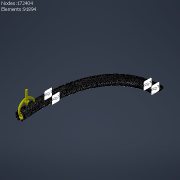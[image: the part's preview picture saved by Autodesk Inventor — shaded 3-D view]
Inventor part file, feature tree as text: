
AUTODESK INVENTOR PART (.ipt)
format: ipt  version: 2021 (Build 250183000, 183)  size: 282,624 bytes
history: native  units: mm
features: sketch x5, sweep x2, extrude x2, plane x2, split x1, hole x1
ambient origin geometry x8: Origin, YZ Plane, XZ Plane, XY Plane, X Axis, Y Axis, Z Axis, Center Point
bodies: Solid1 (feature_tree)
feature tree (13):
  sketch  "Sketch1"  dims[d0=3300.0mm d1=1650.0mm]
  sweep  "Sweep1"
  sweep  "Sweep2"
  extrude  "Extrusion1"  Depth=70.0mm
  extrude  "Extrusion3"  Depth=1650.0mm
  plane  "Work Plane1"
  split  "Split1"
  plane  "Work Plane2"
  hole  "Hole1"  [1 undecoded]
  sketch  "Sketch2"  dims[d2=0.0mm d3=80.0mm]
  sketch  "Sketch3"  dims[d4=0.0mm d5=0.0mm d6=70.0mm]
  sketch  "Sketch4"  dims[d7=0.0mm d8=1650.0mm]
  sketch  "Sketch7"  dims[d9=0.0mm d10=0.0mm d11=1810.0mm d12=3460.0mm d13=1730.0mm d14=1200.0mm d15=1730.0mm d16=1730.0mm d17=200.0mm d18=80.0mm d19=0.0mm d22=14.0mm d23=0.0mm d24=-144.0mm d25=-55.75mm d26=10.0mm d27=6.0mm d28=4.0mm d29=2.0mm d30=90.0deg d31=8.0mm d32=20.594885mm]
note: 1 required parameter value undecoded (feature->parameter linkage not recoverable at this tier; creation-order binding heuristic only, values carry confidence <= 0.55)
